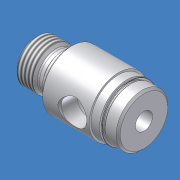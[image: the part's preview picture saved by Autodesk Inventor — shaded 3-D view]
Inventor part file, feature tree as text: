
AUTODESK INVENTOR PART (.ipt)
format: ipt  version: 2012 (Build 160160000, 160)  size: 240,640 bytes
history: native  units: mm (DEFAULTED — no unit token found)
features: other x106, revolve x6, sketch x6, thread x1
ambient origin geometry x8: Origin, YZ Plane, XZ Plane, XY Plane, X Axis, Y Axis, Z Axis, Center Point
bodies: Solid1 (feature_tree)
feature tree (119):
  other  "04RQ000_rod_guide"
  revolve  "Revolution1"  [1 undecoded]
  thread  "Thread1"  [1 undecoded]
  revolve  "Revolution2"  Angle=360.0deg
  revolve  "Revolution3"  Angle=360.0deg
  revolve  "Revolution4"  [1 undecoded]
  revolve  "Revolution5"  [1 undecoded]
  revolve  "Revolution6"  [1 undecoded]
  other  "s1_XY"
  other  "s1_YZ"
  other  "s1_ZX"
  other  "s1_X"
  other  "s1_Y"
  other  "s1_Z"
  other  "s1_Center"
  other  "s2_XY"
  other  "s2_YZ"
  other  "s2_ZX"
  other  "s2_X"
  other  "s2_Y"
  other  "s2_Z"
  other  "s2_Center"
  other  "dp1_XY"
  other  "dp1_YZ"
  other  "dp1_ZX"
  other  "dp1_X"
  other  "dp1_Y"
  other  "dp1_Z"
  other  "dp1_Center"
  other  "dp2_XY"
  other  "dp2_YZ"
  other  "dp2_ZX"
  other  "dp2_X"
  other  "dp2_Y"
  other  "dp2_Z"
  other  "dp2_Center"
  other  "rod_guide_XY"
  other  "rod_guide_YZ"
  other  "rod_guide_ZX"
  other  "rod_guide_X"
  other  "rod_guide_Y"
  other  "rod_guide_Z"
  other  "rod_guide_Center"
  other  "to_tube_XY"
  other  "to_tube_YZ"
  other  "to_tube_ZX"
  other  "to_tube_X"
  other  "to_tube_Y"
  other  "to_tube_Z"
  other  "to_tube_Center"
  other  "to_foot_bracket_XY"
  other  "to_foot_bracket_YZ"
  other  "to_foot_bracket_ZX"
  other  "to_foot_bracket_X"
  other  "to_foot_bracket_Y"
  other  "to_foot_bracket_Z"
  other  "to_foot_bracket_Center"
  other  "to_nut_XY"
  other  "to_nut_YZ"
  other  "to_nut_ZX"
  other  "to_nut_X"
  other  "to_nut_Y"
  other  "to_nut_Z"
  other  "to_nut_Center"
  other  "to_trunnion_brackets_XY"
  other  "to_trunnion_brackets_YZ"
  other  "to_trunnion_brackets_ZX"
  other  "to_trunnion_brackets_X"
  other  "to_trunnion_brackets_Y"
  other  "to_trunnion_brackets_Z"
  other  "to_trunnion_brackets_Center"
  other  "to_trunnion_brackets1_XY"
  other  "to_trunnion_brackets1_YZ"
  other  "to_trunnion_brackets1_ZX"
  other  "to_trunnion_brackets1_X"
  other  "to_trunnion_brackets1_Y"
  other  "to_trunnion_brackets1_Z"
  other  "to_trunnion_brackets1_Center"
  other  "to_trunnion_brackets2_XY"
  other  "to_trunnion_brackets2_YZ"
  other  "to_trunnion_brackets2_ZX"
  other  "to_trunnion_brackets2_X"
  other  "to_trunnion_brackets2_Y"
  other  "to_trunnion_brackets2_Z"
  other  "to_trunnion_brackets2_Center"
  other  "t111_XY"
  other  "t111_YZ"
  other  "t111_ZX"
  other  "t111_X"
  other  "t111_Y"
  other  "t111_Z"
  other  "t111_Center"
  other  "t1_XY"
  other  "t1_YZ"
  other  "t1_ZX"
  other  "t1_X"
  other  "t1_Y"
  other  "t1_Z"
  other  "t1_Center"
  other  "port_XY"
  other  "port_YZ"
  other  "port_ZX"
  other  "port_X"
  other  "port_Y"
  other  "port_Z"
  other  "port_Center"
  other  "to_screw_XY"
  other  "to_screw_YZ"
  other  "to_screw_ZX"
  other  "to_screw_X"
  other  "to_screw_Y"
  other  "to_screw_Z"
  other  "to_screw_Center"
  sketch  "Sketch_2"  dims[d0=360.0deg d1=5.842127mm d2=0.0mm d3=360.0deg]
  sketch  "Sketch_3"  dims[d4=360.0deg d5=360.0deg]
  sketch  "Sketch_5"  dims[d6=360.0deg d7=360.0deg]
  sketch  "Sketch_10"
  sketch  "Sketch_40"
  sketch  "Sketch_47"
note: 5 required parameter values undecoded (feature->parameter linkage not recoverable at this tier; creation-order binding heuristic only, values carry confidence <= 0.55)